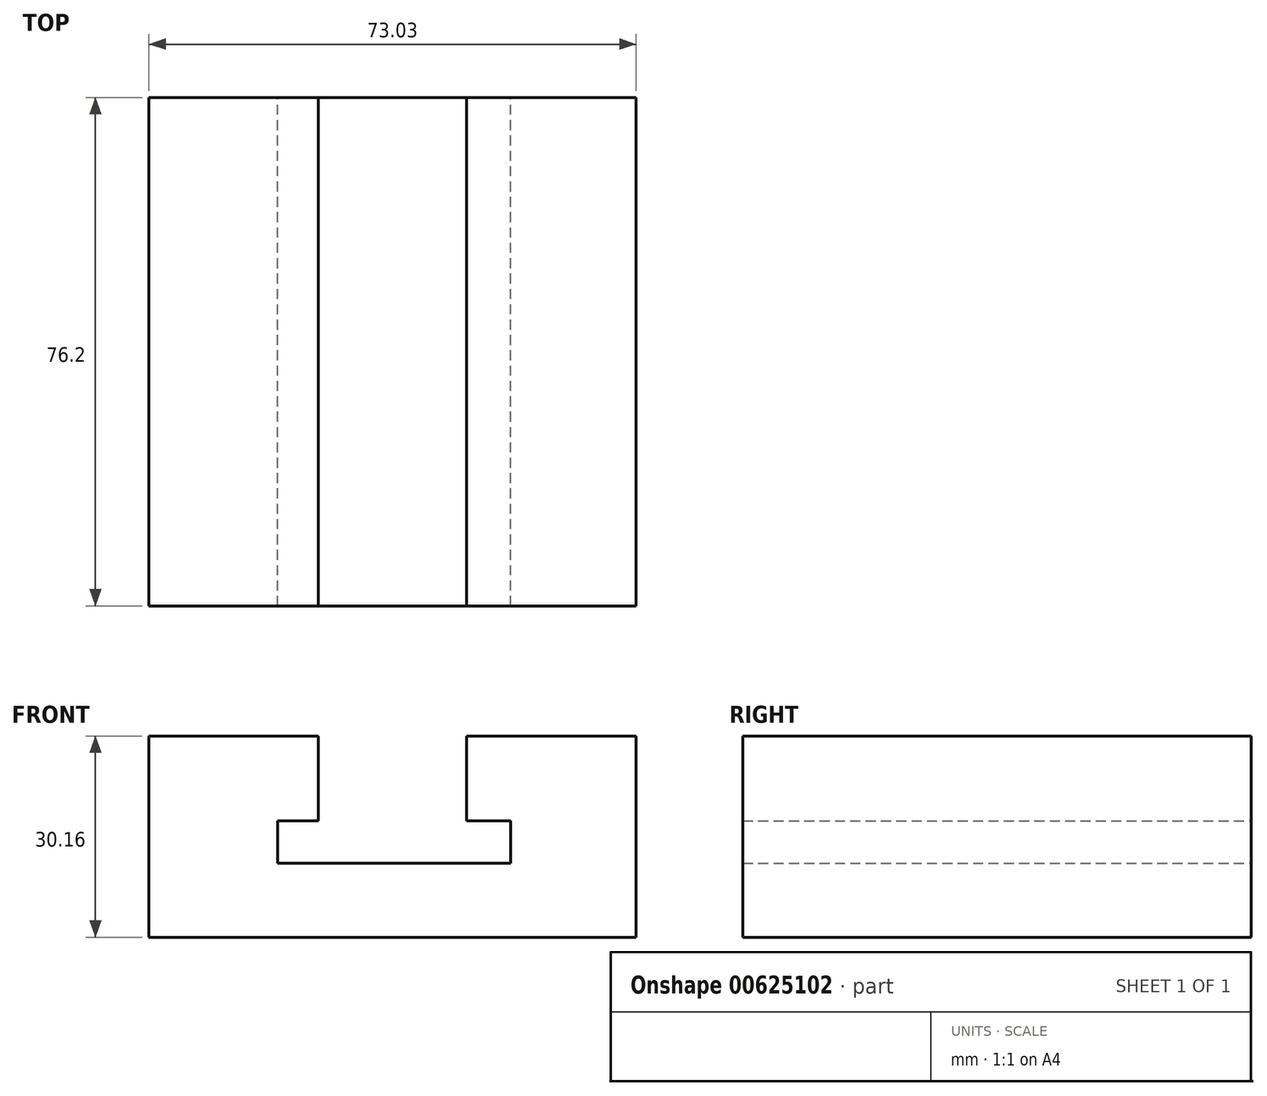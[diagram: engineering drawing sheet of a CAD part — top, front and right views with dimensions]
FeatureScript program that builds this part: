
annotation { "Feature Type Name" : "Feature", "Feature Type Description" : "" }
export const myFeature = defineFeature(function(context is Context, id is Id, definition is map)
    precondition{}
    {
        {
            var Q0;
            Q0=qCreatedBy(makeId("Front.planeOp"),FACE);
            var sketch = newSketch(context, id + "F0", { "sketchPlane" : qUnion([Q0])});
            skLineSegment(sketch, "E0", {"start": v(0, 0) * mm, "end": v(73.03, 0) * mm});
            skLineSegment(sketch, "E1", {"start": v(0, 0) * mm, "end": v(0, 30.16) * mm});
            skLineSegment(sketch, "E2", {"start": v(73.03, 0) * mm, "end": v(73.03, 30.16) * mm});
            skLineSegment(sketch, "E3", {"start": v(0, 30.16) * mm, "end": v(25.4, 30.16) * mm});
            skLineSegment(sketch, "E4", {"start": v(73.03, 30.16) * mm, "end": v(47.62, 30.16) * mm});
            skLineSegment(sketch, "E5", {"start": v(47.62, 30.16) * mm, "end": v(47.62, 17.46) * mm});
            skLineSegment(sketch, "E6", {"start": v(25.4, 30.16) * mm, "end": v(25.4, 17.46) * mm});
            skLineSegment(sketch, "E7", {"start": v(25.4, 17.46) * mm, "end": v(19.32, 17.46) * mm});
            skLineSegment(sketch, "E8", {"start": v(19.32, 17.46) * mm, "end": v(19.32, 11.11) * mm});
            skLineSegment(sketch, "E9", {"start": v(19.32, 11.11) * mm, "end": v(54.24, 11.11) * mm});
            skLineSegment(sketch, "E10", {"start": v(54.24, 11.11) * mm, "end": v(54.24, 17.46) * mm});
            skLineSegment(sketch, "E11", {"start": v(54.24, 17.46) * mm, "end": v(47.62, 17.46) * mm});
            skSolve(sketch);
        }
        {
            var Q0;
            Q0 = qSketchRegion(id + "F0", true);
            extrude(context, id + "F1", {"entities" : qUnion([Q0]), "depth" : 76.2 * mm, "offsetDistance" : 25.4 * mm});
        }
    });
